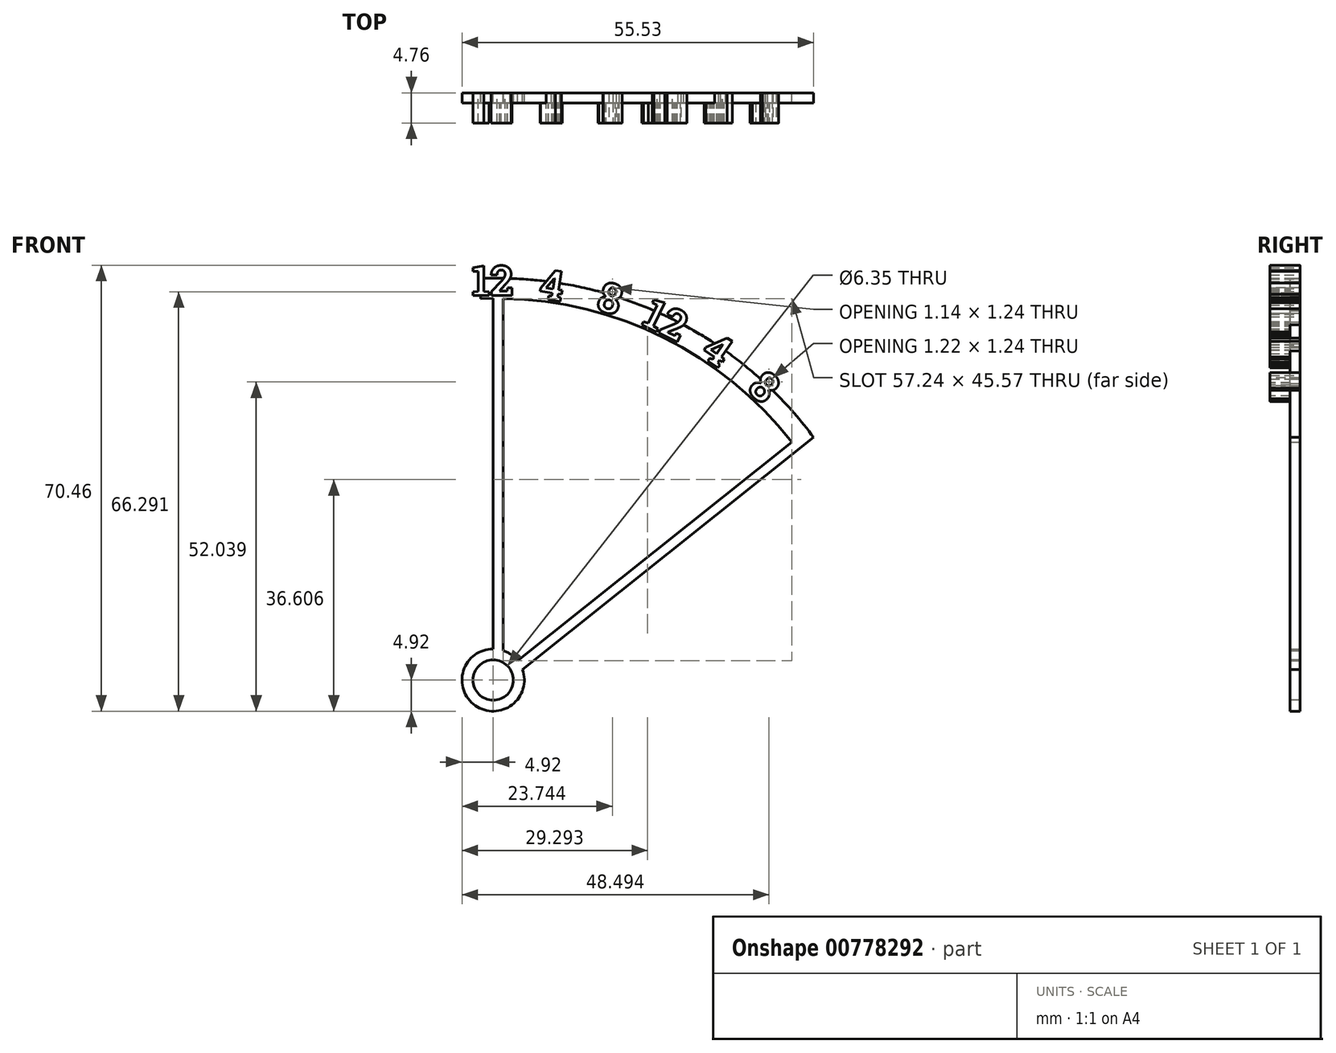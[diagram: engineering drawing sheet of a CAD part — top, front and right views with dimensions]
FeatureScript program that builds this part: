
annotation { "Feature Type Name" : "Feature", "Feature Type Description" : "" }
export const myFeature = defineFeature(function(context is Context, id is Id, definition is map)
    precondition{}
    {
        {
            var Q0;
            Q0=qCreatedBy(makeId("Front.planeOp"),FACE);
            var sketch = newSketch(context, id + "F0", { "sketchPlane" : qUnion([Q0])});
            skCircle(sketch, "E0", {"center": v(0, 0) * mm, "radius": 68.7 * mm, "construction": true});
            skCircle(sketch, "E1", {"center": v(0, 0) * mm, "radius": 65.53 * mm, "construction": true});
            skCircle(sketch, "E2", {"center": v(0, 0) * mm, "radius": 59.18 * mm, "construction": true});
            skLineSegment(sketch, "E3", {"start": v(0, 0) * mm, "end": v(0, 60.77) * mm, "construction": true});
            skLineSegment(sketch, "E4", {"start": v(0, 0) * mm, "end": v(9.77, 64.8) * mm, "construction": true});
            skLineSegment(sketch, "E5", {"start": v(0, 0) * mm, "end": v(19.31, 62.62) * mm, "construction": true});
            skLineSegment(sketch, "E6", {"start": v(0, 0) * mm, "end": v(28.43, 59.04) * mm, "construction": true});
            skLineSegment(sketch, "E7", {"start": v(0, 0) * mm, "end": v(36.91, 54.15) * mm, "construction": true});
            skLineSegment(sketch, "E8", {"start": v(0, 0) * mm, "end": v(44.57, 48.04) * mm, "construction": true});
            skText(sketch, "E9", { "text": "12", "fontName": "RobotoSlab-Bold.ttf"});
            skText(sketch, "E10", { "text": "4", "fontName": "RobotoSlab-Bold.ttf"});
            skText(sketch, "E11", { "text": "8", "fontName": "RobotoSlab-Bold.ttf"});
            skText(sketch, "E12", { "text": "12", "fontName": "RobotoSlab-Bold.ttf"});
            skText(sketch, "E13", { "text": "4", "fontName": "RobotoSlab-Bold.ttf"});
            skText(sketch, "E14", { "text": "8", "fontName": "RobotoSlab-Bold.ttf"});
            const initialGuessF0  = {"E9": [-0.00339, 0.06077, 1, 0, 0.00476], "E10": [0.0071, 0.06037, 0.98883, -0.14902, 0.00478], "E11": [0.01607, 0.05862, 0.95559, -0.2947, 0.00478], "E12": [0.0233, 0.05622, 0.901, -0.43382, 0.00478], "E13": [0.03258, 0.05132, 0.8263, -0.56324, 0.00478], "E14": [0.03991, 0.04585, 0.73314, -0.68008, 0.00478]};
            skSetInitialGuess(sketch, initialGuessF0);
            skSolve(sketch);
        }
        {
            var Q0;
            Q0 = qSketchRegion(id + "F0", true);
            extrude(context, id + "F1", {"entities" : qUnion([Q0]), "depth" : 4.76 * mm, "offsetDistance" : 25.4 * mm});
        }
        {
            var Q0;
            Q0=qCreatedBy(makeId("Front.planeOp"),FACE);
            var sketch = newSketch(context, id + "F2", { "sketchPlane" : qUnion([Q0])});
            skCircle(sketch, "E15", {"center": v(0, 0) * mm, "radius": 4.92 * mm});
            skCircle(sketch, "E16", {"center": v(0, 0) * mm, "radius": 63.5 * mm, "construction": true});
            skLineSegment(sketch, "E17", {"start": v(0, 0) * mm, "end": v(0, 60.3) * mm, "construction": true});
            skLineSegment(sketch, "E18", {"start": v(0, 0) * mm, "end": v(49.64, 39.6) * mm, "construction": true});
            skLineSegment(sketch, "E19", {"start": v(1.59, 63.48) * mm, "end": v(1.59, 4.66) * mm});
            skLineSegment(sketch, "E20", {"start": v(4.63, 1.66) * mm, "end": v(50.61, 38.35) * mm, "construction": true});
            skLineSegment(sketch, "E21", {"start": v(4.63, 1.66) * mm, "end": v(50.61, 38.35) * mm});
            skLineSegment(sketch, "E22", {"start": v(3.85, 3.07) * mm, "end": v(49.64, 39.6) * mm});
            skArc(sketch, "E23", {"start": v(47.16, 37.62) * mm, "mid": v(26.93, 54.1) * mm, "end": v(1.59, 60.3) * mm});
            skArc(sketch, "E24", {"start": v(50.61, 38.35) * mm, "mid": v(28.34, 57.02) * mm, "end": v(0, 63.5) * mm});
            skArc(sketch, "E25", {"start": v(0, 63.5) * mm, "mid": v(-0.97, 63.5) * mm, "end": v(-1.93, 63.47) * mm});
            skLineSegment(sketch, "E26", {"start": v(-1.93, 63.47) * mm, "end": v(-1.99, 60.3) * mm});
            skLineSegment(sketch, "E27", {"start": v(0, 4.92) * mm, "end": v(0, 60.3) * mm});
            skLineSegment(sketch, "E28", {"start": v(-1.99, 60.3) * mm, "end": v(0, 60.3) * mm});
            skSolve(sketch);
        }
        {
            var Q0;
            {var subQ5=sQuery(id+"F2.wireOp",EDGE,"E21");Q0=makeQuery(id+"F2.imprint","IMPRINT",FACE,{"disambiguationData":[TD([[makeQuery(id+"F2.imprint","IMPRINT",EDGE,{"derivedFrom":subQ5}),1.0]])]});}
            var Q1;
            {var subQ0=sQuery(id+"F2.wireOp",EDGE,"E15");var subQ1=makeQuery(id+"F2.imprint","INTERSECT",VERTEX,{"derivedFrom":[subQ0,sQuery(id+"F2.wireOp",EDGE,"E21")]});Q1=makeQuery(id+"F2.imprint","IMPRINT",FACE,{"disambiguationData":[TD([[makeQuery(id+"F2.imprint","IMPRINT",EDGE,{"disambiguationData":[TD([[subQ1,-1.0]])],"derivedFrom":subQ0}),1.0]])]});}
            extrude(context, id + "F3", {"entities" : qUnion([Q0, Q1]), "operationType" : NewBodyOperationType.ADD, "depth" : 1.59 * mm, "offsetDistance" : 25.4 * mm});
        }
        {
            var Q0;
            {var subQ0=sQuery(id+"F2.wireOp",EDGE,"E21");var subQ1=sQuery(id+"F2.wireOp",EDGE,"E19");var subQ2=sQuery(id+"F2.wireOp",EDGE,"E15");var subQ3=sQuery(id+"F2.wireOp",EDGE,"E27");var subQ4=sQuery(id+"F2.wireOp",EDGE,"E22");var subQ5=sQuery(id+"F2.wireOp",EDGE,"E25");var subQ6=sQuery(id+"F2.wireOp",EDGE,"E24");var subQ7=sQuery(id+"F2.wireOp",EDGE,"E23");var subQ8=sQuery(id+"F2.wireOp",EDGE,"E26");var subQ9=sQuery(id+"F2.wireOp",EDGE,"E28");Q0=makeQuery(id+"F3.boolean.opBoolean","SPLIT",FACE,{"disambiguationData":[TD([makeQuery(id+"F1.opExtrude","SWEPT_FACE",FACE,{"disambiguationData":[OSD([sQuery(id+"F0.wireOp",EDGE,"E9.sketch_text.stroke-5")])]})])],"derivedFrom":makeQuery(id+"F3.opExtrude","CAP_FACE",FACE,{"disambiguationData":[OSD([subQ2,subQ1,subQ0,subQ4,subQ7,subQ6,subQ5,subQ8,subQ3,subQ9])],"isStart":false})});}
            var sketch = newSketch(context, id + "F4", { "sketchPlane" : qUnion([Q0])});
            skPoint(sketch, "E29", {"position": v(0, 0) * mm});
            skPoint(sketch, "E30", {"position": v(0, 1.66) * mm});
            skSolve(sketch);
        }
        {
            var Q0;
            Q0=sQuery(id+"F4.wireOp",VERTEX,"E29");
            var Q1;
            Q1=makeQuery(id+"F1.opExtrude","SWEPT_BODY",BODY,{"disambiguationData":[OSD([sQuery(id+"F0.wireOp",EDGE,"E9.sketch_text.stroke-0"),sQuery(id+"F0.wireOp",EDGE,"E9.sketch_text.stroke-1"),sQuery(id+"F0.wireOp",EDGE,"E9.sketch_text.stroke-2"),sQuery(id+"F0.wireOp",EDGE,"E9.sketch_text.stroke-3"),sQuery(id+"F0.wireOp",EDGE,"E9.sketch_text.stroke-4"),sQuery(id+"F0.wireOp",EDGE,"E9.sketch_text.stroke-5"),sQuery(id+"F0.wireOp",EDGE,"E9.sketch_text.stroke-6"),sQuery(id+"F0.wireOp",EDGE,"E9.sketch_text.stroke-7"),sQuery(id+"F0.wireOp",EDGE,"E9.sketch_text.stroke-8"),sQuery(id+"F0.wireOp",EDGE,"E9.sketch_text.stroke-9")])]});
            hole(context, id + "F5", {"style" : HoleStyle.SIMPLE, "endStyle" : HoleEndStyle.THROUGH, "holeDiameter" : 6.35 * mm, "majorDiameter" : 6.35 * mm, "isTappedThrough" : true, "tappedDepth" : 12.7 * mm, "tapClearance" : 3, "locations" : qUnion([Q0]), "scope" : qUnion([Q1])});
        }
    });
